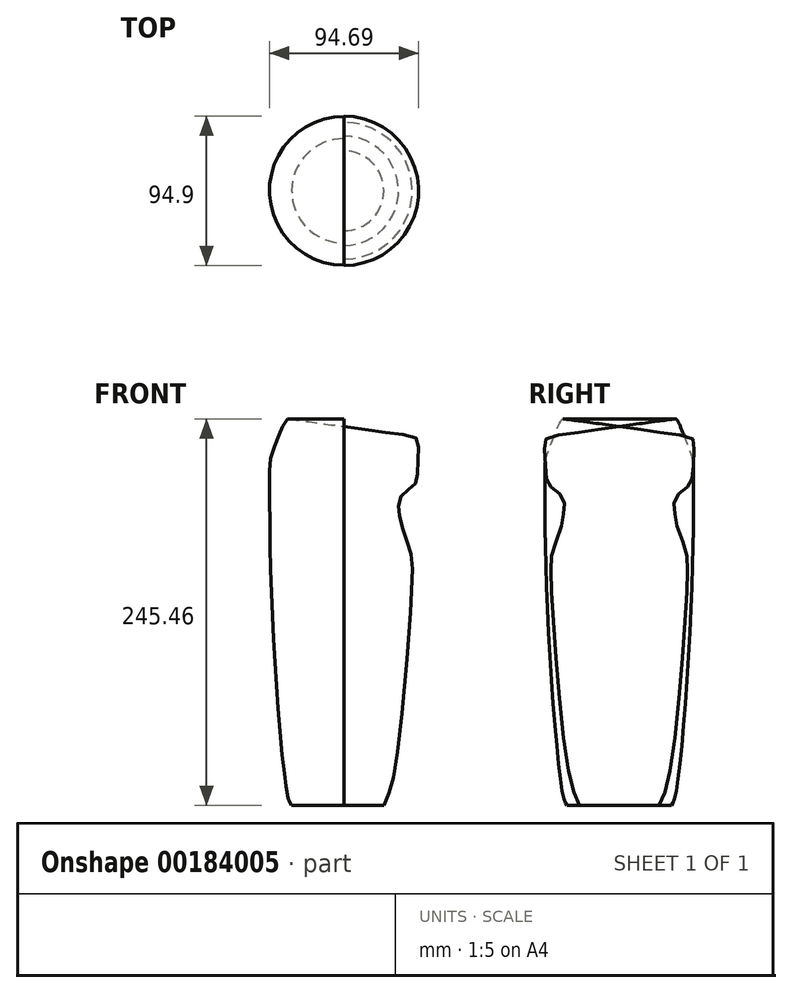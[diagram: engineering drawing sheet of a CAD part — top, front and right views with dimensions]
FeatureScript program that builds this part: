
annotation { "Feature Type Name" : "Feature", "Feature Type Description" : "" }
export const myFeature = defineFeature(function(context is Context, id is Id, definition is map)
    precondition{}
    {
        {
            var Q0;
            Q0=qCreatedBy(makeId("Front.planeOp"),FACE);
            var sketch = newSketch(context, id + "F0", { "sketchPlane" : qUnion([Q0])});
            skLineSegment(sketch, "E0", {"start": v(0, 93.8) * mm, "end": v(0, -146.8) * mm});
            skPoint(sketch, "E0.endSnap0", {"position": v(0, -150) * mm});
            skLineSegment(sketch, "E1", {"start": v(0, -146.8) * mm, "end": v(-33.15, -146.8) * mm});
            skFitSpline(sketch, "E2", {"points": [v(-33.15, -146.8) * mm, v(-35.44, -141.58) * mm, v(-46.32, -3.19) * mm, v(-47.18, 65.62) * mm, v(-46.32, 74.38) * mm, v(-36.83, 97.97) * mm, v(-35.61, 98.64) * mm, v(0, 93.8) * mm], "startDerivative": vector(-35.2, 46.1) * mm, "endDerivative": vector(303.99, -43.85) * mm});
            skLineSegment(sketch, "E3", {"start": v(0, -146.8) * mm, "end": v(25.35, -146.8) * mm});
            skFitSpline(sketch, "E4", {"points": [v(25.35, -146.8) * mm, v(31.25, -130.04) * mm, v(40.95, -42.7) * mm, v(43.44, 4.22) * mm, v(41.73, 16.4) * mm, v(36.2, 32.77) * mm, v(35.07, 40.39) * mm, v(35.26, 47.81) * mm, v(40.97, 53.71) * mm, v(45.35, 57.71) * mm, v(46.87, 66.47) * mm, v(47.44, 82.08) * mm, v(46.03, 86.4) * mm, v(26.69, 90.03) * mm, v(0, 93.8) * mm], "startDerivative": vector(82.58, 171.6) * mm, "endDerivative": vector(-360.62, 44.86) * mm});
            skSolve(sketch);
        }
        {
            var Q0;
            Q0=makeQuery(id+"F0.imprint","IMPRINT",FACE,{"disambiguationData":[TD([[makeQuery(id+"F0.imprint","IMPRINT",EDGE,{"derivedFrom":sQuery(id+"F0.wireOp",EDGE,"E0")}),-1.0]])]});
            var Q1;
            Q1=sQuery(id+"F0.wireOp",EDGE,"E0");
            revolve(context, id + "F1", {"entities" : qUnion([Q0]), "axis" : qUnion([Q1]), "revolveType" : RevolveType.TWO_DIRECTIONS, "angle" : 90 * degree, "angleBack" : 270 * degree});
        }
        {
            var Q0;
            Q0=makeQuery(id+"F0.imprint","IMPRINT",FACE,{"disambiguationData":[TD([[makeQuery(id+"F0.imprint","IMPRINT",EDGE,{"derivedFrom":sQuery(id+"F0.wireOp",EDGE,"E0")}),1.0]])]});
            var Q1;
            Q1=sQuery(id+"F0.wireOp",EDGE,"E0");
            revolve(context, id + "F2", {"entities" : qUnion([Q0]), "axis" : qUnion([Q1]), "revolveType" : RevolveType.TWO_DIRECTIONS, "angle" : 90 * degree, "angleBack" : 270 * degree});
        }
    });
